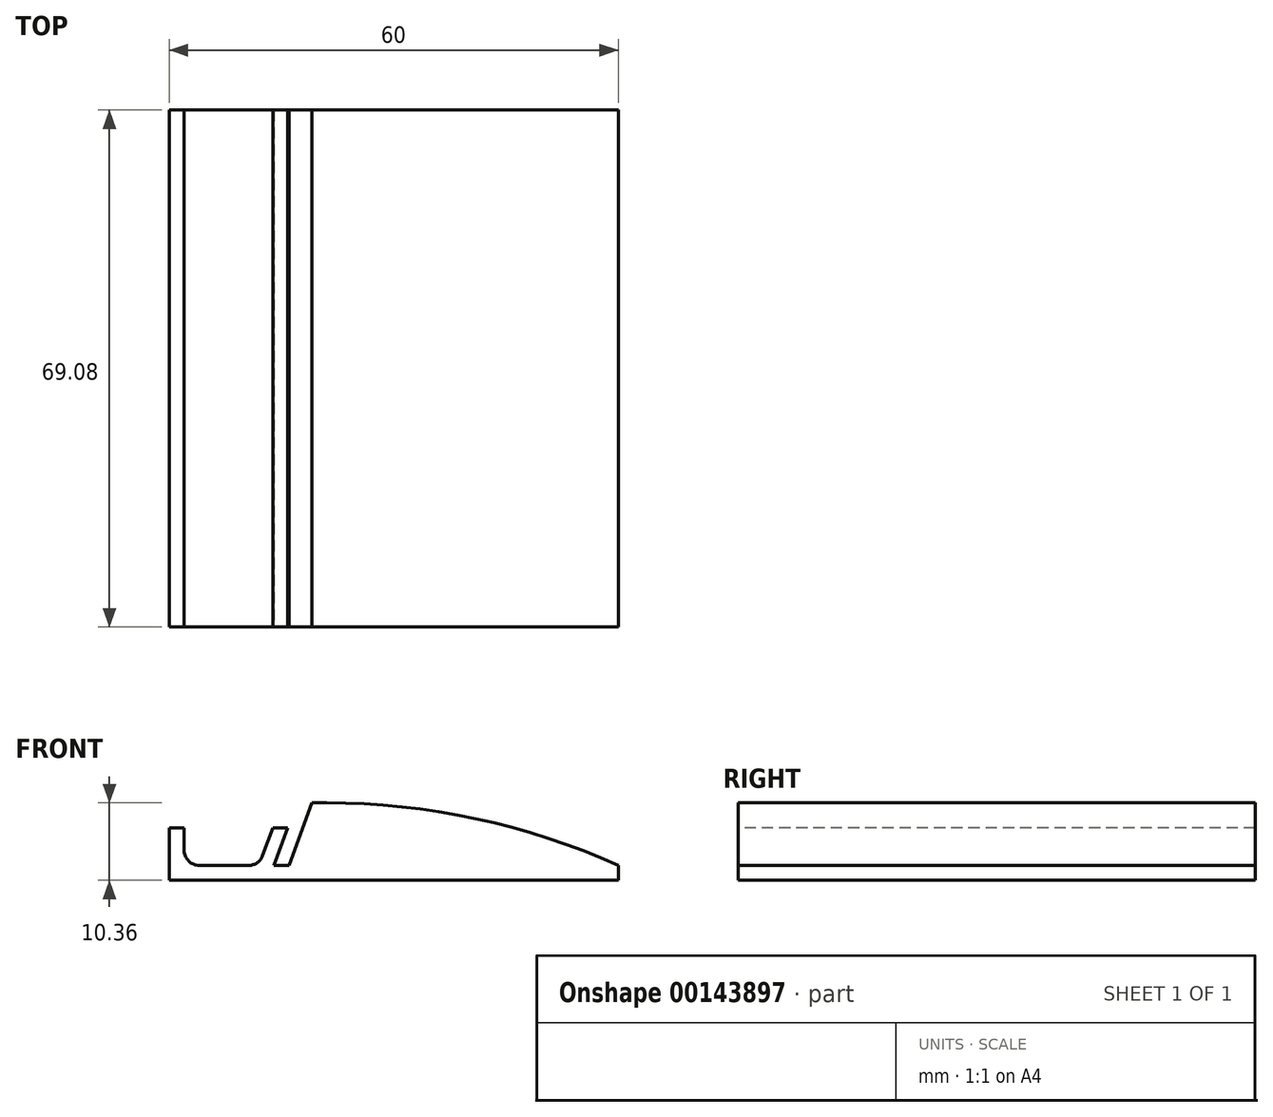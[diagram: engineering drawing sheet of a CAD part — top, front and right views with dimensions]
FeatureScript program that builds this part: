
annotation { "Feature Type Name" : "Feature", "Feature Type Description" : "" }
export const myFeature = defineFeature(function(context is Context, id is Id, definition is map)
    precondition{}
    {
        {
            var Q0;
            Q0=qCreatedBy(makeId("Front.planeOp"),FACE);
            var sketch = newSketch(context, id + "F0", { "sketchPlane" : qUnion([Q0])});
            skLineSegment(sketch, "E0", {"start": v(0, 0) * mm, "end": v(0, -2) * mm});
            skLineSegment(sketch, "E1", {"start": v(0, -2) * mm, "end": v(-60, -2) * mm});
            skLineSegment(sketch, "E2", {"start": v(-60, -2) * mm, "end": v(-60, 5) * mm});
            skLineSegment(sketch, "E3", {"start": v(-60, 5) * mm, "end": v(-58, 5) * mm});
            skLineSegment(sketch, "E4", {"start": v(-58, 5) * mm, "end": v(-58, 0) * mm});
            skLineSegment(sketch, "E5", {"start": v(-58, 0) * mm, "end": v(-48, 0) * mm});
            skLineSegment(sketch, "E6", {"start": v(-48, 0) * mm, "end": v(-46.18, 5) * mm});
            skLineSegment(sketch, "E7", {"start": v(-46.18, 5) * mm, "end": v(-44.18, 5) * mm});
            skLineSegment(sketch, "E8", {"start": v(-44.18, 5) * mm, "end": v(-46, 0) * mm});
            skLineSegment(sketch, "E9", {"start": v(-46, 0) * mm, "end": v(-44, 0) * mm});
            skLineSegment(sketch, "E10", {"start": v(-44, 0) * mm, "end": v(-40.96, 8.36) * mm});
            skLineSegment(sketch, "E11", {"start": v(-40.96, 8.36) * mm, "end": v(-38.96, 8.36) * mm});
            skArc(sketch, "E12", {"start": v(0, 0) * mm, "mid": v(-19.04, 6.24) * mm, "end": v(-38.96, 8.36) * mm});
            skSolve(sketch);
        }
        {
            var Q0;
            Q0=makeQuery(id+"F0.imprint","IMPRINT",FACE,{"disambiguationData":[TD([[makeQuery(id+"F0.imprint","IMPRINT",EDGE,{"derivedFrom":sQuery(id+"F0.wireOp",EDGE,"E0")}),-1.0]])]});
            extrude(context, id + "F1", {"entities" : qUnion([Q0]), "oppositeDirection" : true, "depth" : 69.08 * mm});
        }
        {
            var Q0;
            Q0=makeQuery(id+"F1.opExtrude","SWEPT_EDGE",EDGE,{"disambiguationData":[OSD([sQuery(id+"F0.wireOp",EDGE,"E5"),sQuery(id+"F0.wireOp",EDGE,"E6")])]});
            fillet(context, id + "F2", {"entities" : qUnion([Q0]), "radius" : 2 * mm, "tangentPropagation" : true, "allowEdgeOverflow" : false});
        }
        {
            var Q0;
            Q0=makeQuery(id+"F1.opExtrude","SWEPT_EDGE",EDGE,{"disambiguationData":[OSD([sQuery(id+"F0.wireOp",EDGE,"E4"),sQuery(id+"F0.wireOp",EDGE,"E5")])]});
            fillet(context, id + "F3", {"entities" : qUnion([Q0]), "radius" : 2 * mm, "tangentPropagation" : true, "allowEdgeOverflow" : false});
        }
    });
